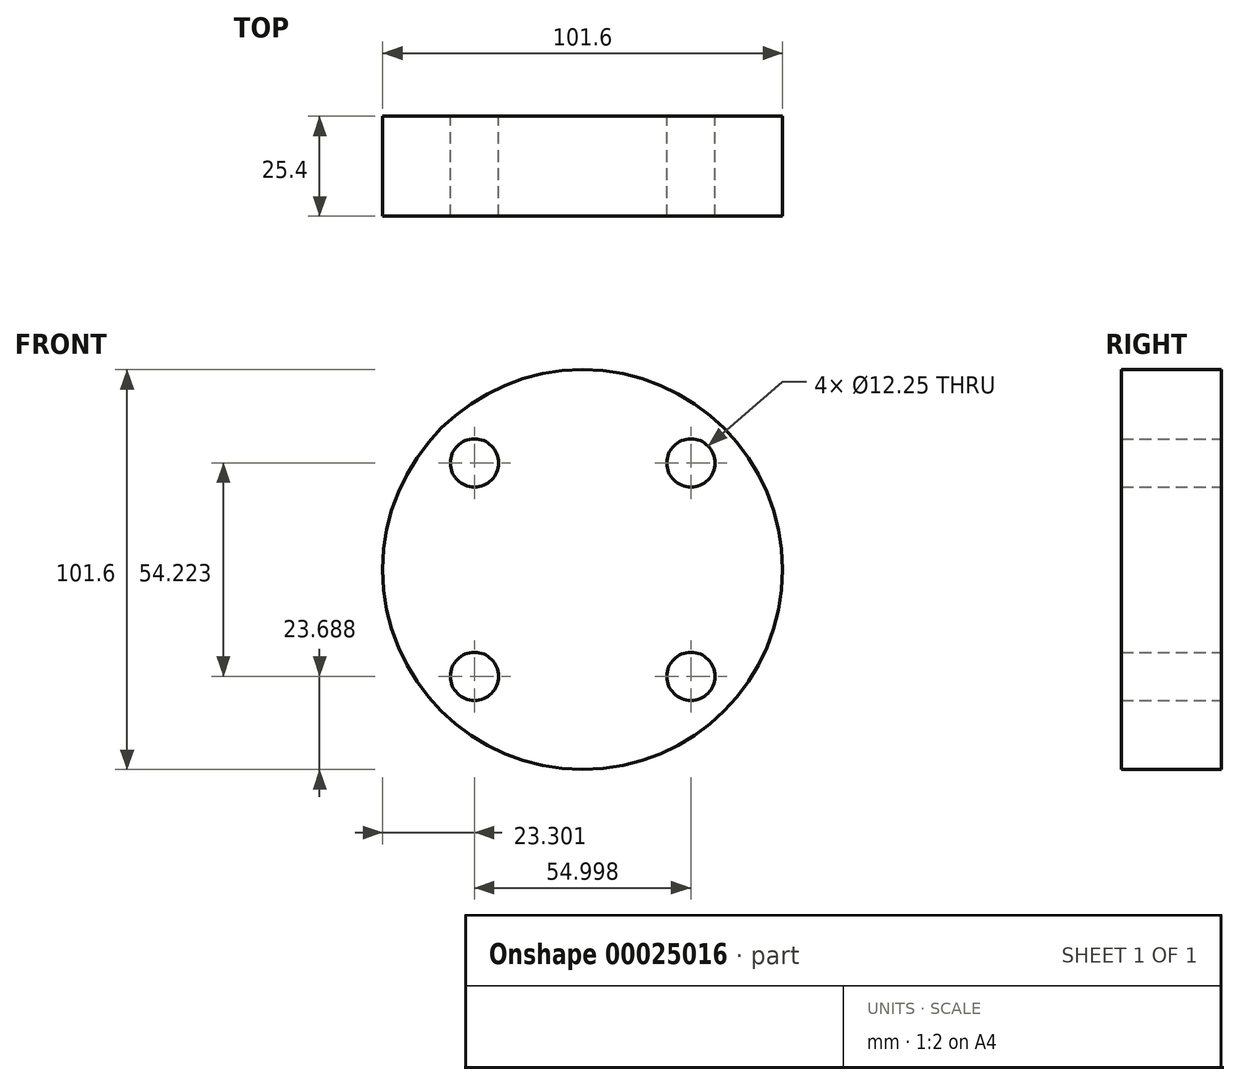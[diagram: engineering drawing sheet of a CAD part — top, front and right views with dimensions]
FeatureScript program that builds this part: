
annotation { "Feature Type Name" : "Feature", "Feature Type Description" : "" }
export const myFeature = defineFeature(function(context is Context, id is Id, definition is map)
    precondition{}
    {
        {
            var Q0;
            Q0=qCreatedBy(makeId("Front.planeOp"),FACE);
            var sketch = newSketch(context, id + "F0", { "sketchPlane" : qUnion([Q0])});
            skCircle(sketch, "E0", {"center": v(0, 0) * mm, "radius": 50.8 * mm});
            skCircle(sketch, "E1", {"center": v(-27.5, 27.11) * mm, "radius": 6.12 * mm});
            skCircle(sketch, "E2.MirrorC", {"center": v(27.5, 27.11) * mm, "radius": 6.12 * mm});
            skCircle(sketch, "E3.MirrorC", {"center": v(-27.5, -27.11) * mm, "radius": 6.12 * mm});
            skCircle(sketch, "E4.MirrorC", {"center": v(27.5, -27.11) * mm, "radius": 6.12 * mm});
            skSolve(sketch);
        }
        {
            var Q0;
            Q0 = qSketchRegion(id + "F0", true);
            extrude(context, id + "F1", {"entities" : qUnion([Q0]), "depth" : 25.4 * mm});
        }
        {
            var Q0;
            Q0=makeQuery(id+"F0.imprint","IMPRINT",FACE,{"disambiguationData":[TD([[makeQuery(id+"F0.imprint","IMPRINT",EDGE,{"derivedFrom":sQuery(id+"F0.wireOp",EDGE,"E1")}),1.0]])]});
            var Q1;
            Q1=makeQuery(id+"F0.imprint","IMPRINT",FACE,{"disambiguationData":[TD([[makeQuery(id+"F0.imprint","IMPRINT",EDGE,{"derivedFrom":sQuery(id+"F0.wireOp",EDGE,"E3.MirrorC")}),-1.0]])]});
            var Q2;
            Q2=makeQuery(id+"F0.imprint","IMPRINT",FACE,{"disambiguationData":[TD([[makeQuery(id+"F0.imprint","IMPRINT",EDGE,{"derivedFrom":sQuery(id+"F0.wireOp",EDGE,"E2.MirrorC")}),-1.0]])]});
            var Q3;
            Q3=makeQuery(id+"F0.imprint","IMPRINT",FACE,{"disambiguationData":[TD([[makeQuery(id+"F0.imprint","IMPRINT",EDGE,{"derivedFrom":sQuery(id+"F0.wireOp",EDGE,"E4.MirrorC")}),1.0]])]});
            var Q4;
            Q4=sQuery(id+"F0.wireOp",EDGE,"E1");
            var Q5;
            Q5=sQuery(id+"F0.wireOp",EDGE,"E3.MirrorC");
            var Q6;
            Q6=sQuery(id+"F0.wireOp",EDGE,"E4.MirrorC");
            var Q7;
            Q7=sQuery(id+"F0.wireOp",EDGE,"E2.MirrorC");
            extrude(context, id + "F2", {"entities" : qUnion([Q0, Q1, Q2, Q3]), "operationType" : NewBodyOperationType.REMOVE, "surfaceEntities" : qUnion([Q4, Q5, Q6, Q7]), "endBound" : BoundingType.THROUGH_ALL, "oppositeDirection" : true, "depth" : 25.4 * mm});
        }
    });
